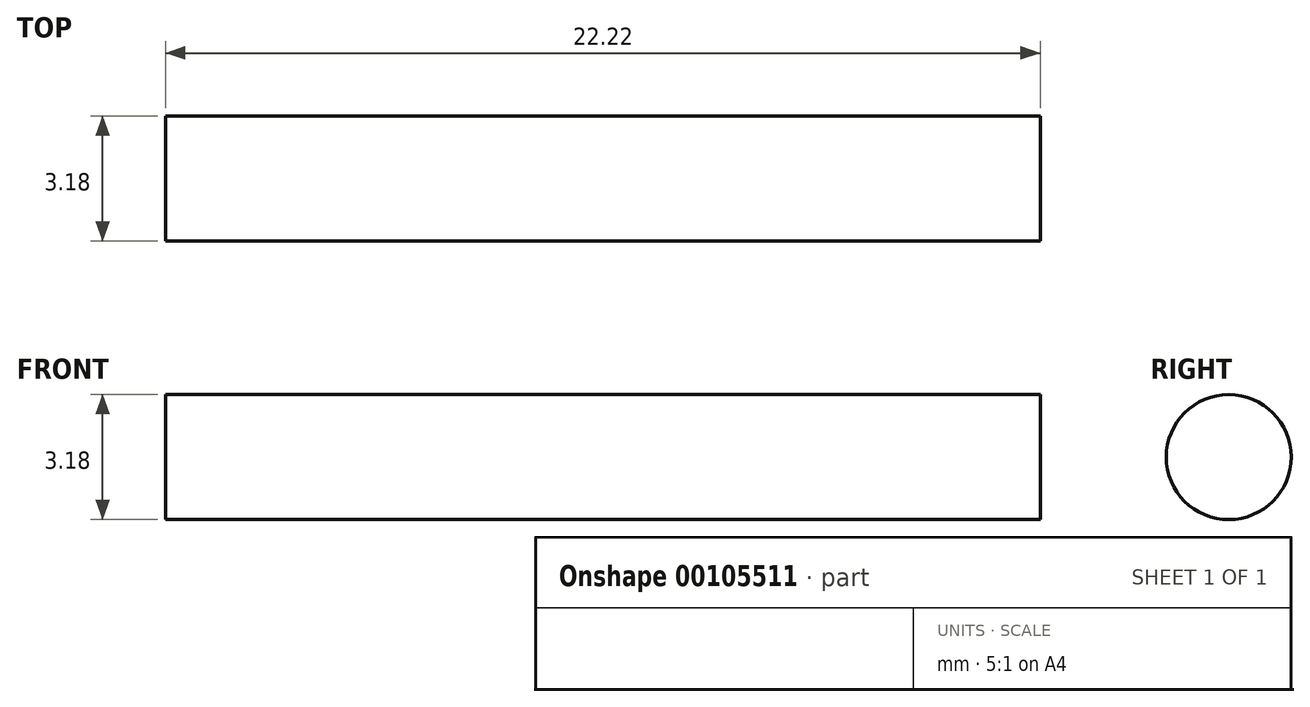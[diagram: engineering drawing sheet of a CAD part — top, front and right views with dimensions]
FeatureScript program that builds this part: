
annotation { "Feature Type Name" : "Feature", "Feature Type Description" : "" }
export const myFeature = defineFeature(function(context is Context, id is Id, definition is map)
    precondition{}
    {
        {
            var Q0;
            Q0=qCreatedBy(makeId("Right.planeOp"),FACE);
            var sketch = newSketch(context, id + "F0", { "sketchPlane" : qUnion([Q0])});
            skCircle(sketch, "E0", {"center": v(0, 0) * mm, "radius": 1.59 * mm});
            skSolve(sketch);
        }
        {
            var Q0;
            Q0=makeQuery(id+"F0.imprint","IMPRINT",FACE,{"disambiguationData":[TD([[makeQuery(id+"F0.imprint","IMPRINT",EDGE,{"derivedFrom":sQuery(id+"F0.wireOp",EDGE,"E0")}),1.0]])]});
            extrude(context, id + "F1", {"entities" : qUnion([Q0]), "endBound" : BoundingType.SYMMETRIC, "depth" : 22.22 * mm});
        }
    });
